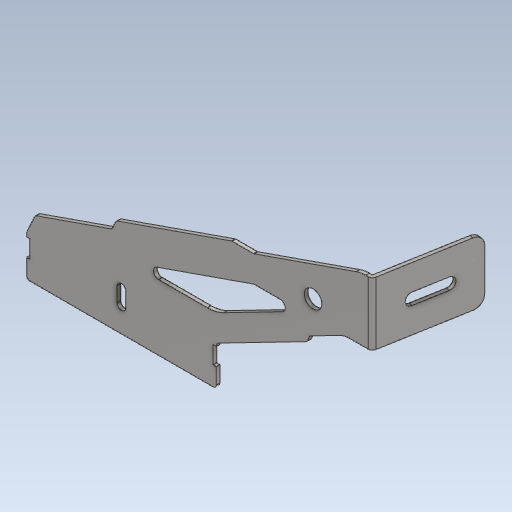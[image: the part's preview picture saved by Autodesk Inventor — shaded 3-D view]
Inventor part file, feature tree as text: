
AUTODESK INVENTOR PART (.ipt)
format: ipt  version: 2020 (Build 240168000, 168)  size: 583,680 bytes
history: native  units: mm
features: other x3, extrude x1, plane x1
ambient origin geometry x8: Origin, YZ Plane, XZ Plane, XY Plane, X Axis, Y Axis, Z Axis, Center Point
bodies: Body1 (feature_tree)
feature tree (5):
  other  "實體1"
  extrude  "擠出1"  Depth=130.0mm
  other  "折彎零件1"
  plane  "工作平面1"
  other  "定義1"
